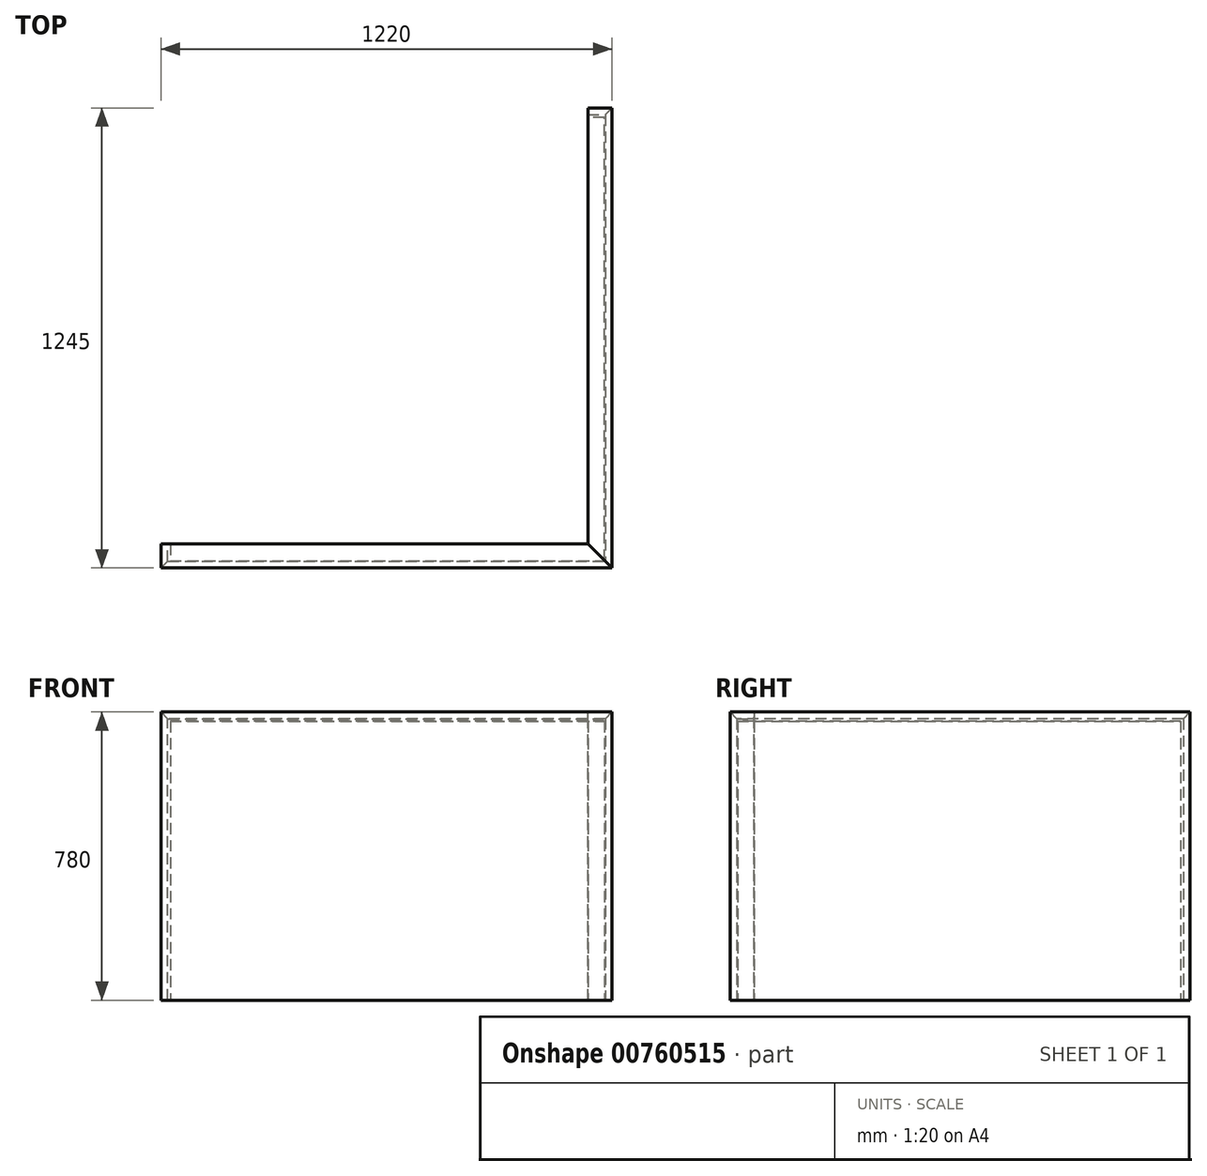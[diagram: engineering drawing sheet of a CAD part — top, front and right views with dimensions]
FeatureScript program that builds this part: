
annotation { "Feature Type Name" : "Feature", "Feature Type Description" : "" }
export const myFeature = defineFeature(function(context is Context, id is Id, definition is map)
    precondition{}
    {
        {
            var Q0;
            Q0=qCreatedBy(makeId("Top.planeOp"),FACE);
            var sketch = newSketch(context, id + "F0", { "sketchPlane" : qUnion([Q0])});
            skLineSegment(sketch, "E0", {"start": v(-1175, 0) * mm, "end": v(0, 0) * mm});
            skLineSegment(sketch, "E1", {"start": v(0, 0) * mm, "end": v(0, 1200) * mm});
            skLineSegment(sketch, "E2", {"start": v(0, 1200) * mm, "end": v(-45, 1200) * mm});
            skLineSegment(sketch, "E3", {"start": v(-45, 1200) * mm, "end": v(-45, 45) * mm});
            skLineSegment(sketch, "E4", {"start": v(-45, 45) * mm, "end": v(-1175, 45) * mm});
            skLineSegment(sketch, "E5", {"start": v(-1175, 45) * mm, "end": v(-1175, 0) * mm});
            skSolve(sketch);
        }
        {
            var Q0;
            Q0=makeQuery(id+"F0.imprint","IMPRINT",FACE,{"disambiguationData":[TD([[makeQuery(id+"F0.imprint","IMPRINT",EDGE,{"derivedFrom":sQuery(id+"F0.wireOp",EDGE,"E0")}),1.0]])]});
            extrude(context, id + "F1", {"entities" : qUnion([Q0]), "depth" : 755 * mm, "offsetDistance" : 25 * mm});
        }
        {
            var Q0;
            Q0=makeQuery(id+"F1.opExtrude","SWEPT_FACE",FACE,{"disambiguationData":[OSD([sQuery(id+"F0.wireOp",EDGE,"E0")])]});
            cPlane(context, id + "F2", {"entities" : qUnion([Q0]), "cplaneType" : CPlaneType.OFFSET, "offset" : 20 * mm, "width" : 150 * mm, "height" : 150 * mm});
        }
        {
            var Q0;
            Q0=qCreatedBy(id+"F2.planeOp",FACE);
            var sketch = newSketch(context, id + "F3", { "sketchPlane" : qUnion([Q0])});
            skLineSegment(sketch, "E6", {"start": v(20, 0) * mm, "end": v(20, 780) * mm});
            skLineSegment(sketch, "E7", {"start": v(20, 780) * mm, "end": v(-1200, 780) * mm});
            skLineSegment(sketch, "E8", {"start": v(-1200, 780) * mm, "end": v(-1200, 0) * mm});
            skLineSegment(sketch, "E9", {"start": v(-1200, 0) * mm, "end": v(20, 0) * mm});
            skSolve(sketch);
        }
        {
            var Q0;
            Q0=makeQuery(id+"F3.imprint","IMPRINT",FACE,{"disambiguationData":[TD([[makeQuery(id+"F3.imprint","IMPRINT",EDGE,{"derivedFrom":sQuery(id+"F3.wireOp",EDGE,"E6")}),1.0]])]});
            extrude(context, id + "F4", {"entities" : qUnion([Q0]), "oppositeDirection" : true, "depth" : 18 * mm, "offsetDistance" : 25 * mm});
        }
        {
            var Q0;
            Q0=makeQuery(id+"F4.opExtrude","CAP_EDGE",EDGE,{"disambiguationData":[OSD([sQuery(id+"F3.wireOp",EDGE,"E6")])],"isStart":false});
            var Q1;
            Q1=makeQuery(id+"F4.opExtrude","CAP_EDGE",EDGE,{"disambiguationData":[OSD([sQuery(id+"F3.wireOp",EDGE,"E7")])],"isStart":false});
            var Q2;
            Q2=makeQuery(id+"F4.opExtrude","CAP_EDGE",EDGE,{"disambiguationData":[OSD([sQuery(id+"F3.wireOp",EDGE,"E8")])],"isStart":false});
            chamfer(context, id + "F5", {"entities" : qUnion([Q0, Q1, Q2]), "width" : 18 * mm, "tangentPropagation" : true});
        }
        {
            var Q0;
            Q0=makeQuery(id+"F1.opExtrude","SWEPT_FACE",FACE,{"disambiguationData":[OSD([sQuery(id+"F0.wireOp",EDGE,"E1")])]});
            cPlane(context, id + "F6", {"entities" : qUnion([Q0]), "cplaneType" : CPlaneType.OFFSET, "offset" : 20 * mm, "width" : 150 * mm, "height" : 150 * mm});
        }
        {
            var Q0;
            Q0=qCreatedBy(id+"F6.planeOp",FACE);
            var sketch = newSketch(context, id + "F7", { "sketchPlane" : qUnion([Q0])});
            skLineSegment(sketch, "E10.bottom", {"start": v(-20, 0) * mm, "end": v(1225, 0) * mm});
            skLineSegment(sketch, "E10.top", {"start": v(-20, 780) * mm, "end": v(1225, 780) * mm});
            skLineSegment(sketch, "E10.left", {"start": v(-20, 0) * mm, "end": v(-20, 780) * mm});
            skLineSegment(sketch, "E10.right", {"start": v(1225, 0) * mm, "end": v(1225, 780) * mm});
            skSolve(sketch);
        }
        {
            var Q0;
            Q0=makeQuery(id+"F7.imprint","IMPRINT",FACE,{"disambiguationData":[TD([[makeQuery(id+"F7.imprint","IMPRINT",EDGE,{"derivedFrom":sQuery(id+"F7.wireOp",EDGE,"E10.bottom")}),1.0]])]});
            extrude(context, id + "F8", {"entities" : qUnion([Q0]), "oppositeDirection" : true, "depth" : 18 * mm, "offsetDistance" : 25 * mm});
        }
        {
            var Q0;
            Q0=makeQuery(id+"F8.opExtrude","CAP_EDGE",EDGE,{"disambiguationData":[OSD([sQuery(id+"F7.wireOp",EDGE,"E10.left")])],"isStart":false});
            var Q1;
            Q1=makeQuery(id+"F8.opExtrude","CAP_EDGE",EDGE,{"disambiguationData":[OSD([sQuery(id+"F7.wireOp",EDGE,"E10.top")])],"isStart":false});
            var Q2;
            Q2=makeQuery(id+"F8.opExtrude","CAP_EDGE",EDGE,{"disambiguationData":[OSD([sQuery(id+"F7.wireOp",EDGE,"E10.right")])],"isStart":false});
            chamfer(context, id + "F9", {"entities" : qUnion([Q0, Q1, Q2]), "width" : 18 * mm, "tangentPropagation" : true});
        }
        {
            var Q0;
            Q0=qCreatedBy(id+"F2.planeOp",FACE);
            var Q1;
            {var subQ0=sQuery(id+"F3.wireOp",EDGE,"E8");Q1=makeQuery(id+"F5.opChamfer","BLEND_EDGE",EDGE,{"blendedFrom":[makeQuery(id+"F4.opExtrude","CAP_EDGE",EDGE,{"disambiguationData":[OSD([subQ0])],"isStart":false}),makeQuery(id+"F4.opExtrude","CAP_FACE",FACE,{"disambiguationData":[OSD([sQuery(id+"F3.wireOp",EDGE,"E6"),sQuery(id+"F3.wireOp",EDGE,"E7"),subQ0,sQuery(id+"F3.wireOp",EDGE,"E9")])],"isStart":true})],"blendedInto":[makeQuery(id+"F4.opExtrude","CAP_FACE",FACE,{"disambiguationData":[OSD([sQuery(id+"F3.wireOp",EDGE,"E6"),sQuery(id+"F3.wireOp",EDGE,"E7"),subQ0,sQuery(id+"F3.wireOp",EDGE,"E9")])],"isStart":true})]});}
            cPlane(context, id + "F10", {"entities" : qUnion([Q0, Q1]), "cplaneType" : CPlaneType.LINE_ANGLE, "offset" : 25 * mm, "angle" : 90 * degree, "width" : 150 * mm, "height" : 150 * mm});
        }
        {
            var Q0;
            Q0=qCreatedBy(id+"F10.planeOp",FACE);
            var sketch = newSketch(context, id + "F11", { "sketchPlane" : qUnion([Q0])});
            skLineSegment(sketch, "E11.bottom", {"start": v(-20, 0) * mm, "end": v(45, 0) * mm});
            skLineSegment(sketch, "E11.top", {"start": v(-20, 780) * mm, "end": v(45, 780) * mm});
            skLineSegment(sketch, "E11.left", {"start": v(-20, 0) * mm, "end": v(-20, 780) * mm});
            skLineSegment(sketch, "E11.right", {"start": v(45, 0) * mm, "end": v(45, 780) * mm});
            skSolve(sketch);
        }
        {
            var Q0;
            Q0=makeQuery(id+"F11.imprint","IMPRINT",FACE,{"disambiguationData":[TD([[makeQuery(id+"F11.imprint","IMPRINT",EDGE,{"derivedFrom":sQuery(id+"F11.wireOp",EDGE,"E11.bottom")}),1.0]])]});
            extrude(context, id + "F12", {"entities" : qUnion([Q0]), "depth" : 18 * mm, "offsetDistance" : 25 * mm});
        }
        {
            var Q0;
            Q0=makeQuery(id+"F12.opExtrude","CAP_EDGE",EDGE,{"disambiguationData":[OSD([sQuery(id+"F11.wireOp",EDGE,"E11.top")])],"isStart":false});
            var Q1;
            Q1=makeQuery(id+"F12.opExtrude","CAP_EDGE",EDGE,{"disambiguationData":[OSD([sQuery(id+"F11.wireOp",EDGE,"E11.left")])],"isStart":false});
            chamfer(context, id + "F13", {"entities" : qUnion([Q0, Q1]), "width" : 18 * mm, "tangentPropagation" : true});
        }
        {
            var Q0;
            Q0=qCreatedBy(id+"F6.planeOp",FACE);
            var Q1;
            {var subQ0=sQuery(id+"F7.wireOp",EDGE,"E10.right");Q1=makeQuery(id+"F9.opChamfer","BLEND_EDGE",EDGE,{"blendedFrom":[makeQuery(id+"F8.opExtrude","CAP_EDGE",EDGE,{"disambiguationData":[OSD([subQ0])],"isStart":false}),makeQuery(id+"F8.opExtrude","CAP_FACE",FACE,{"disambiguationData":[OSD([sQuery(id+"F7.wireOp",EDGE,"E10.bottom"),sQuery(id+"F7.wireOp",EDGE,"E10.top"),sQuery(id+"F7.wireOp",EDGE,"E10.left"),subQ0])],"isStart":true})],"blendedInto":[makeQuery(id+"F8.opExtrude","CAP_FACE",FACE,{"disambiguationData":[OSD([sQuery(id+"F7.wireOp",EDGE,"E10.bottom"),sQuery(id+"F7.wireOp",EDGE,"E10.top"),sQuery(id+"F7.wireOp",EDGE,"E10.left"),subQ0])],"isStart":true})]});}
            cPlane(context, id + "F14", {"entities" : qUnion([Q0, Q1]), "cplaneType" : CPlaneType.LINE_ANGLE, "offset" : 25 * mm, "angle" : 90 * degree, "width" : 150 * mm, "height" : 150 * mm});
        }
        {
            var Q0;
            Q0=qCreatedBy(id+"F14.planeOp",FACE);
            var sketch = newSketch(context, id + "F15", { "sketchPlane" : qUnion([Q0])});
            skLineSegment(sketch, "E12.bottom", {"start": v(20, 0) * mm, "end": v(-45, 0) * mm});
            skLineSegment(sketch, "E12.top", {"start": v(20, 780) * mm, "end": v(-45, 780) * mm});
            skLineSegment(sketch, "E12.left", {"start": v(20, 0) * mm, "end": v(20, 780) * mm});
            skLineSegment(sketch, "E12.right", {"start": v(-45, 0) * mm, "end": v(-45, 780) * mm});
            skSolve(sketch);
        }
        {
            var Q0;
            Q0=makeQuery(id+"F15.imprint","IMPRINT",FACE,{"disambiguationData":[TD([[makeQuery(id+"F15.imprint","IMPRINT",EDGE,{"derivedFrom":sQuery(id+"F15.wireOp",EDGE,"E12.bottom")}),-1.0]])]});
            extrude(context, id + "F16", {"entities" : qUnion([Q0]), "depth" : 18 * mm, "offsetDistance" : 25 * mm});
        }
        {
            var Q0;
            Q0=makeQuery(id+"F16.opExtrude","CAP_EDGE",EDGE,{"disambiguationData":[OSD([sQuery(id+"F15.wireOp",EDGE,"E12.left")])],"isStart":false});
            var Q1;
            Q1=makeQuery(id+"F16.opExtrude","CAP_EDGE",EDGE,{"disambiguationData":[OSD([sQuery(id+"F15.wireOp",EDGE,"E12.top")])],"isStart":false});
            chamfer(context, id + "F17", {"entities" : qUnion([Q0, Q1]), "width" : 18 * mm, "tangentPropagation" : true});
        }
        {
            var Q0;
            Q0=makeQuery(id+"F8.opExtrude","CAP_FACE",FACE,{"disambiguationData":[OSD([sQuery(id+"F7.wireOp",EDGE,"E10.bottom"),sQuery(id+"F7.wireOp",EDGE,"E10.top"),sQuery(id+"F7.wireOp",EDGE,"E10.left"),sQuery(id+"F7.wireOp",EDGE,"E10.right")])],"isStart":true});
            var Q1;
            {var subQ0=sQuery(id+"F7.wireOp",EDGE,"E10.top");Q1=makeQuery(id+"F9.opChamfer","BLEND_EDGE",EDGE,{"blendedFrom":[makeQuery(id+"F8.opExtrude","CAP_EDGE",EDGE,{"disambiguationData":[OSD([subQ0])],"isStart":false}),makeQuery(id+"F8.opExtrude","CAP_FACE",FACE,{"disambiguationData":[OSD([sQuery(id+"F7.wireOp",EDGE,"E10.bottom"),subQ0,sQuery(id+"F7.wireOp",EDGE,"E10.left"),sQuery(id+"F7.wireOp",EDGE,"E10.right")])],"isStart":true})],"blendedInto":[makeQuery(id+"F8.opExtrude","CAP_FACE",FACE,{"disambiguationData":[OSD([sQuery(id+"F7.wireOp",EDGE,"E10.bottom"),subQ0,sQuery(id+"F7.wireOp",EDGE,"E10.left"),sQuery(id+"F7.wireOp",EDGE,"E10.right")])],"isStart":true})]});}
            cPlane(context, id + "F18", {"entities" : qUnion([Q0, Q1]), "cplaneType" : CPlaneType.LINE_ANGLE, "offset" : 25 * mm, "angle" : 90 * degree, "width" : 150 * mm, "height" : 150 * mm});
        }
        {
            var Q0;
            Q0=qCreatedBy(id+"F18.planeOp",FACE);
            var sketch = newSketch(context, id + "F19", { "sketchPlane" : qUnion([Q0])});
            skLineSegment(sketch, "E13", {"start": v(20, -20) * mm, "end": v(20, 1225) * mm});
            skLineSegment(sketch, "E14", {"start": v(20, 1225) * mm, "end": v(-45, 1225) * mm});
            skLineSegment(sketch, "E15", {"start": v(-45, 1225) * mm, "end": v(-45, 45) * mm});
            skLineSegment(sketch, "E16", {"start": v(-45, 45) * mm, "end": v(20, -20) * mm});
            skSolve(sketch);
        }
        {
            var Q0;
            Q0=makeQuery(id+"F4.opExtrude","CAP_FACE",FACE,{"disambiguationData":[OSD([sQuery(id+"F3.wireOp",EDGE,"E6"),sQuery(id+"F3.wireOp",EDGE,"E7"),sQuery(id+"F3.wireOp",EDGE,"E8"),sQuery(id+"F3.wireOp",EDGE,"E9")])],"isStart":true});
            var Q1;
            {var subQ0=sQuery(id+"F3.wireOp",EDGE,"E7");Q1=makeQuery(id+"F5.opChamfer","BLEND_EDGE",EDGE,{"blendedFrom":[makeQuery(id+"F4.opExtrude","CAP_EDGE",EDGE,{"disambiguationData":[OSD([subQ0])],"isStart":false}),makeQuery(id+"F4.opExtrude","CAP_FACE",FACE,{"disambiguationData":[OSD([sQuery(id+"F3.wireOp",EDGE,"E6"),subQ0,sQuery(id+"F3.wireOp",EDGE,"E8"),sQuery(id+"F3.wireOp",EDGE,"E9")])],"isStart":true})],"blendedInto":[makeQuery(id+"F4.opExtrude","CAP_FACE",FACE,{"disambiguationData":[OSD([sQuery(id+"F3.wireOp",EDGE,"E6"),subQ0,sQuery(id+"F3.wireOp",EDGE,"E8"),sQuery(id+"F3.wireOp",EDGE,"E9")])],"isStart":true})]});}
            cPlane(context, id + "F20", {"entities" : qUnion([Q0, Q1]), "cplaneType" : CPlaneType.LINE_ANGLE, "offset" : 25 * mm, "angle" : 90 * degree, "width" : 150 * mm, "height" : 150 * mm});
        }
        {
            var Q0;
            Q0=qCreatedBy(id+"F20.planeOp",FACE);
            var sketch = newSketch(context, id + "F21", { "sketchPlane" : qUnion([Q0])});
            skLineSegment(sketch, "E17", {"start": v(-1200, -45) * mm, "end": v(-1200, 20) * mm});
            skLineSegment(sketch, "E18", {"start": v(-1200, 20) * mm, "end": v(20, 20) * mm});
            skLineSegment(sketch, "E19", {"start": v(20, 20) * mm, "end": v(-45, -45) * mm});
            skLineSegment(sketch, "E20", {"start": v(-45, -45) * mm, "end": v(-1200, -45) * mm});
            skSolve(sketch);
        }
        {
            var Q0;
            Q0=makeQuery(id+"F21.imprint","IMPRINT",FACE,{"disambiguationData":[TD([[makeQuery(id+"F21.imprint","IMPRINT",EDGE,{"derivedFrom":sQuery(id+"F21.wireOp",EDGE,"E17")}),-1.0]])]});
            extrude(context, id + "F22", {"entities" : qUnion([Q0]), "depth" : 18 * mm, "offsetDistance" : 25 * mm});
        }
        {
            var Q0;
            Q0=makeQuery(id+"F19.imprint","IMPRINT",FACE,{"disambiguationData":[TD([[makeQuery(id+"F19.imprint","IMPRINT",EDGE,{"derivedFrom":sQuery(id+"F19.wireOp",EDGE,"E13")}),1.0]])]});
            extrude(context, id + "F23", {"entities" : qUnion([Q0]), "oppositeDirection" : true, "depth" : 18 * mm, "offsetDistance" : 25 * mm});
        }
        {
            var Q0;
            Q0=makeQuery(id+"F22.opExtrude","CAP_EDGE",EDGE,{"disambiguationData":[OSD([sQuery(id+"F21.wireOp",EDGE,"E17")])],"isStart":false});
            var Q1;
            Q1=makeQuery(id+"F22.opExtrude","CAP_EDGE",EDGE,{"disambiguationData":[OSD([sQuery(id+"F21.wireOp",EDGE,"E18")])],"isStart":false});
            var Q2;
            Q2=makeQuery(id+"F23.opExtrude","CAP_EDGE",EDGE,{"disambiguationData":[OSD([sQuery(id+"F19.wireOp",EDGE,"E13")])],"isStart":false});
            var Q3;
            Q3=makeQuery(id+"F23.opExtrude","CAP_EDGE",EDGE,{"disambiguationData":[OSD([sQuery(id+"F19.wireOp",EDGE,"E14")])],"isStart":false});
            chamfer(context, id + "F24", {"entities" : qUnion([Q0, Q1, Q2, Q3]), "width" : 18 * mm, "tangentPropagation" : true});
        }
    });
